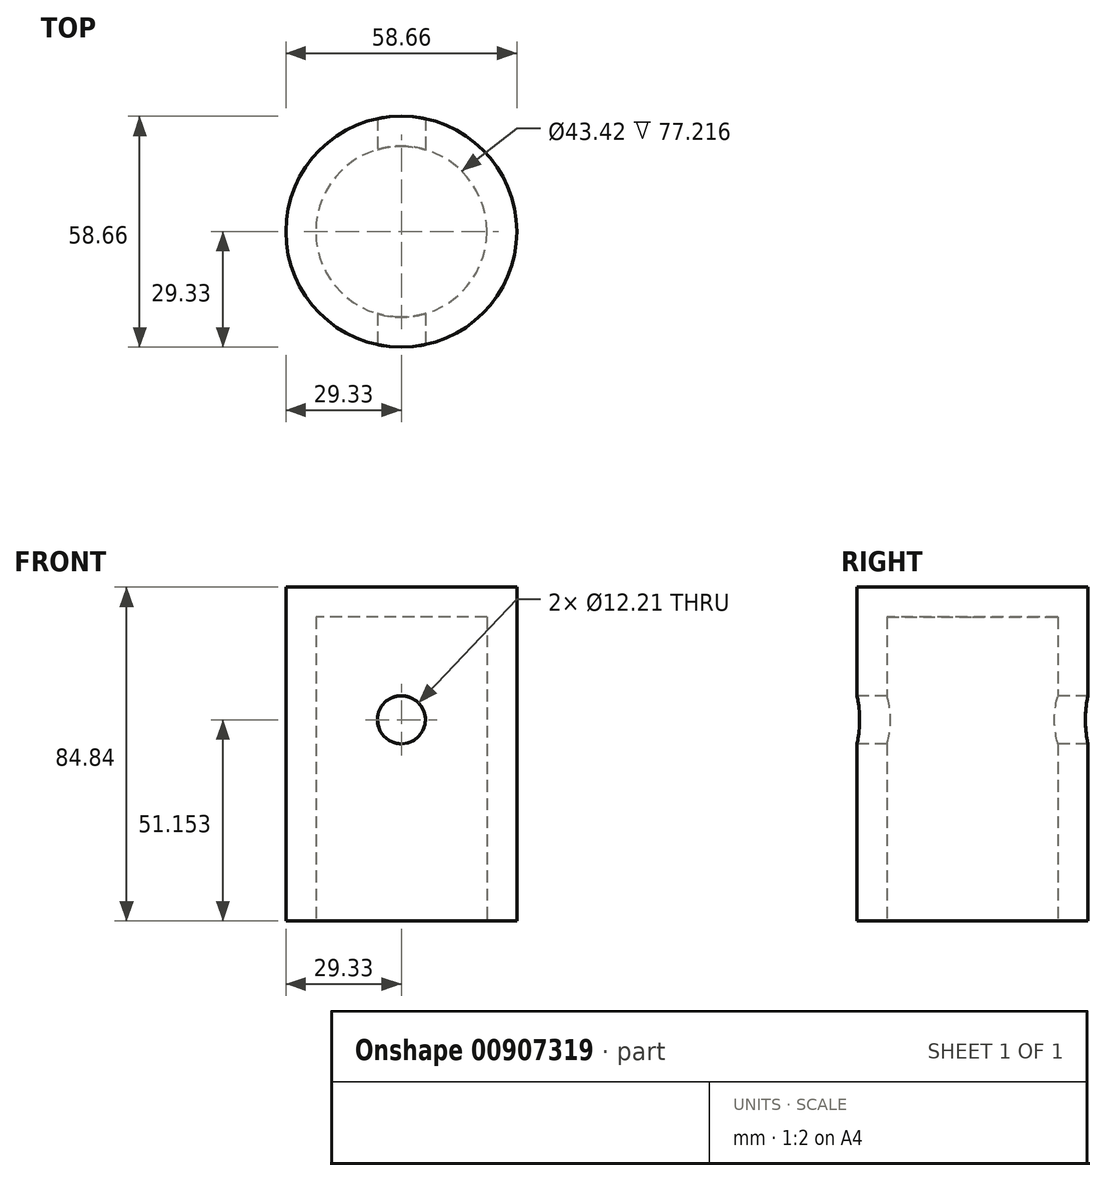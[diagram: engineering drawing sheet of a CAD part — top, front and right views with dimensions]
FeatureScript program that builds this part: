
annotation { "Feature Type Name" : "Feature", "Feature Type Description" : "" }
export const myFeature = defineFeature(function(context is Context, id is Id, definition is map)
    precondition{}
    {
        {
            var Q0;
            Q0=qCreatedBy(makeId("Top.planeOp"),FACE);
            var sketch = newSketch(context, id + "F0", { "sketchPlane" : qUnion([Q0])});
            skCircle(sketch, "E0", {"center": v(0, 0) * mm, "radius": 29.33 * mm});
            skSolve(sketch);
        }
        {
            var Q0;
            Q0=makeQuery(id+"F0.imprint","IMPRINT",FACE,{"disambiguationData":[TD([[makeQuery(id+"F0.imprint","IMPRINT",EDGE,{"derivedFrom":sQuery(id+"F0.wireOp",EDGE,"E0")}),1.0]])]});
            extrude(context, id + "F1", {"entities" : qUnion([Q0]), "depth" : 84.84 * mm, "offsetDistance" : 25.4 * mm});
        }
        {
            var Q0;
            Q0=makeQuery(id+"F1.opExtrude","CAP_FACE",FACE,{"disambiguationData":[OSD([sQuery(id+"F0.wireOp",EDGE,"E0")])],"isStart":true});
            shell(context, id + "F2", {"entities" : qUnion([Q0]), "thickness" : 7.62 * mm});
        }
        {
            var Q0;
            Q0=qCreatedBy(makeId("Front.planeOp"),FACE);
            var sketch = newSketch(context, id + "F3", { "sketchPlane" : qUnion([Q0])});
            skCircle(sketch, "E1", {"center": v(0, 51.15) * mm, "radius": 6.1 * mm});
            skSolve(sketch);
        }
        {
            var Q0;
            Q0 = qSketchRegion(id + "F3", true);
            extrude(context, id + "F4", {"entities" : qUnion([Q0]), "operationType" : NewBodyOperationType.REMOVE, "endBound" : BoundingType.THROUGH_ALL, "oppositeDirection" : true, "depth" : 25.4 * mm, "offsetDistance" : 25.4 * mm, "hasSecondDirection" : true, "secondDirectionBound" : SecondDirectionBoundingType.THROUGH_ALL, "secondDirectionOppositeDirection" : false, "secondDirectionDepth" : 25.4 * mm});
        }
    });
